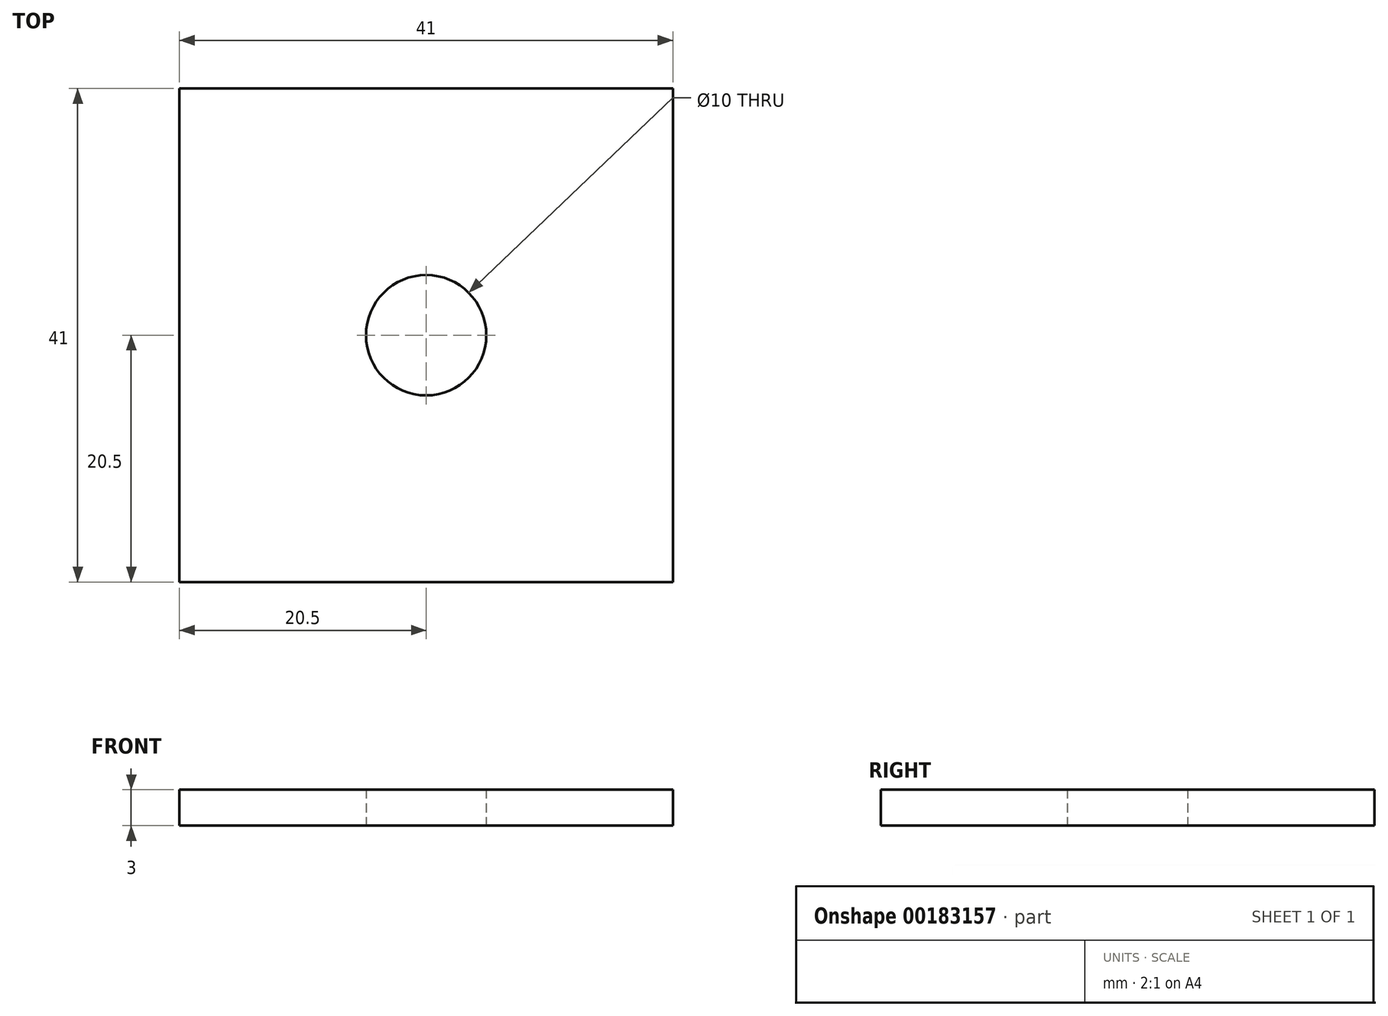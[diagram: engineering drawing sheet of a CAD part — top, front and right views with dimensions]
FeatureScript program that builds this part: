
annotation { "Feature Type Name" : "Feature", "Feature Type Description" : "" }
export const myFeature = defineFeature(function(context is Context, id is Id, definition is map)
    precondition{}
    {
        {
            var Q0;
            Q0=qCreatedBy(makeId("Top.planeOp"),FACE);
            var sketch = newSketch(context, id + "F0", { "sketchPlane" : qUnion([Q0])});
            skLineSegment(sketch, "E0.bottom", {"start": v(0, 0) * mm, "end": v(41, 0) * mm});
            skLineSegment(sketch, "E0.top", {"start": v(0, 41) * mm, "end": v(41, 41) * mm});
            skLineSegment(sketch, "E0.left", {"start": v(0, 0) * mm, "end": v(0, 41) * mm});
            skLineSegment(sketch, "E0.right", {"start": v(41, 0) * mm, "end": v(41, 41) * mm});
            skCircle(sketch, "E1", {"center": v(20.5, 20.5) * mm, "radius": 5 * mm});
            skPoint(sketch, "E1.centerSnap0", {"position": v(41, 20.5) * mm});
            skPoint(sketch, "E1.centerSnap1", {"position": v(20.5, 41) * mm});
            skSolve(sketch);
        }
        {
            var Q0;
            Q0 = qSketchRegion(id + "F0", true);
            extrude(context, id + "F1", {"entities" : qUnion([Q0]), "depth" : 3 * mm});
        }
    });
